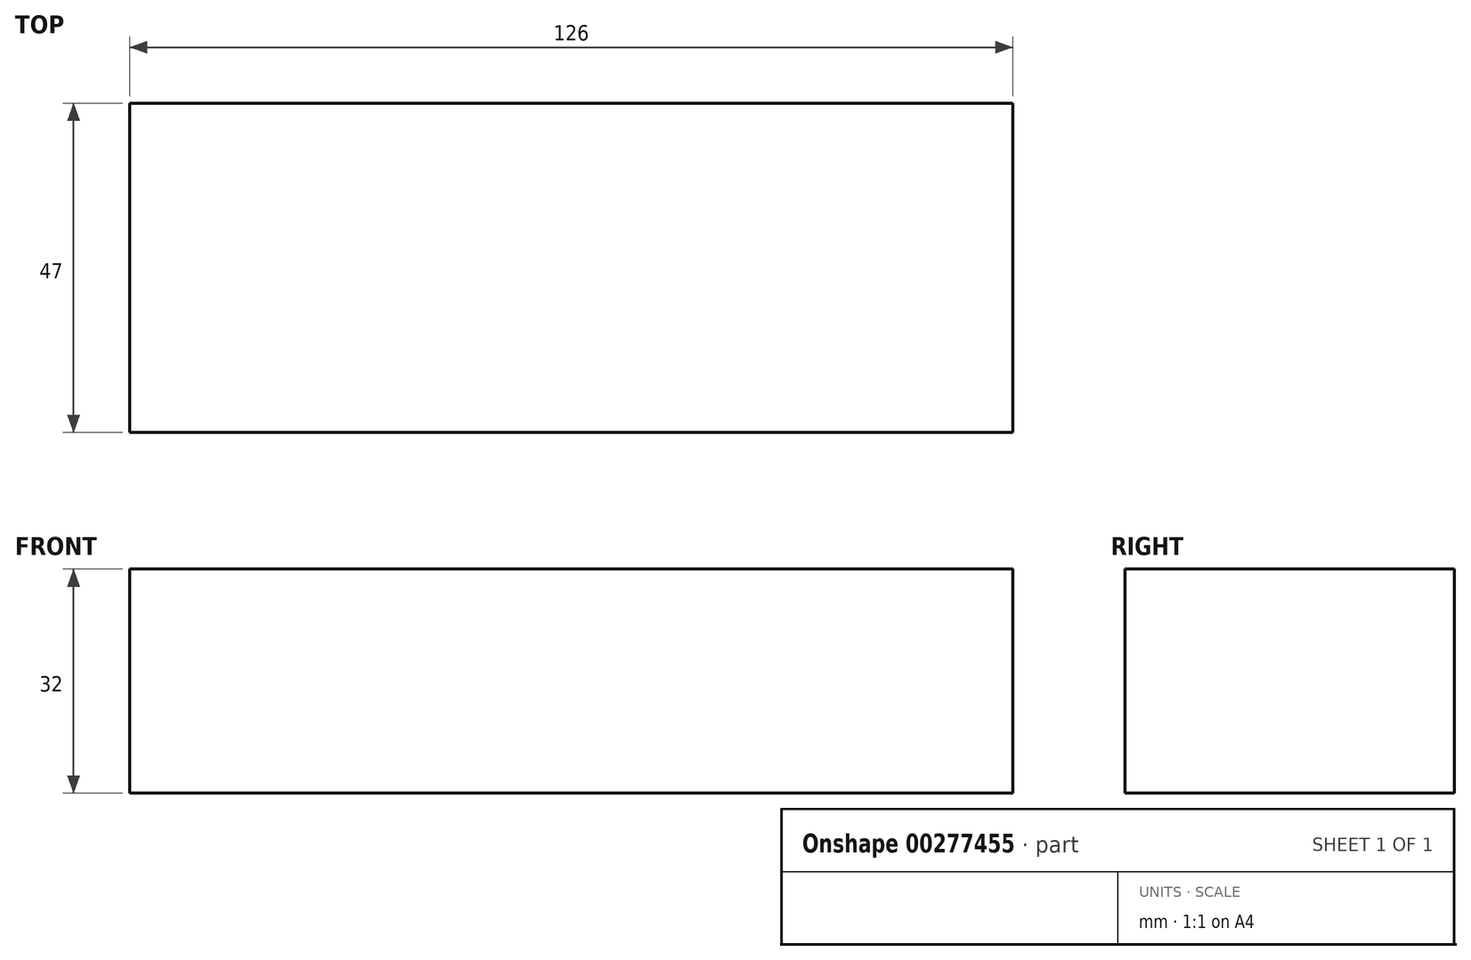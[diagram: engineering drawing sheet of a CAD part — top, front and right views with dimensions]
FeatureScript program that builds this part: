
annotation { "Feature Type Name" : "Feature", "Feature Type Description" : "" }
export const myFeature = defineFeature(function(context is Context, id is Id, definition is map)
    precondition{}
    {
        {
            var Q0;
            Q0=qCreatedBy(makeId("Top.planeOp"),FACE);
            var sketch = newSketch(context, id + "F0", { "sketchPlane" : qUnion([Q0])});
            skLineSegment(sketch, "E0.bottom", {"start": v(63, 23.5) * mm, "end": v(-63, 23.5) * mm});
            skLineSegment(sketch, "E0.top", {"start": v(63, -23.5) * mm, "end": v(-63, -23.5) * mm});
            skLineSegment(sketch, "E0.left", {"start": v(63, 23.5) * mm, "end": v(63, -23.5) * mm});
            skLineSegment(sketch, "E0.right", {"start": v(-63, 23.5) * mm, "end": v(-63, -23.5) * mm});
            skPoint(sketch, "E0.middle", {"position": v(0, 0) * mm});
            skSolve(sketch);
        }
        {
            var Q0;
            Q0=makeQuery(id+"F0.imprint","IMPRINT",FACE,{"disambiguationData":[TD([[makeQuery(id+"F0.imprint","IMPRINT",EDGE,{"derivedFrom":sQuery(id+"F0.wireOp",EDGE,"E0.bottom")}),1.0]])]});
            extrude(context, id + "F1", {"entities" : qUnion([Q0]), "depth" : 32 * mm});
        }
    });
